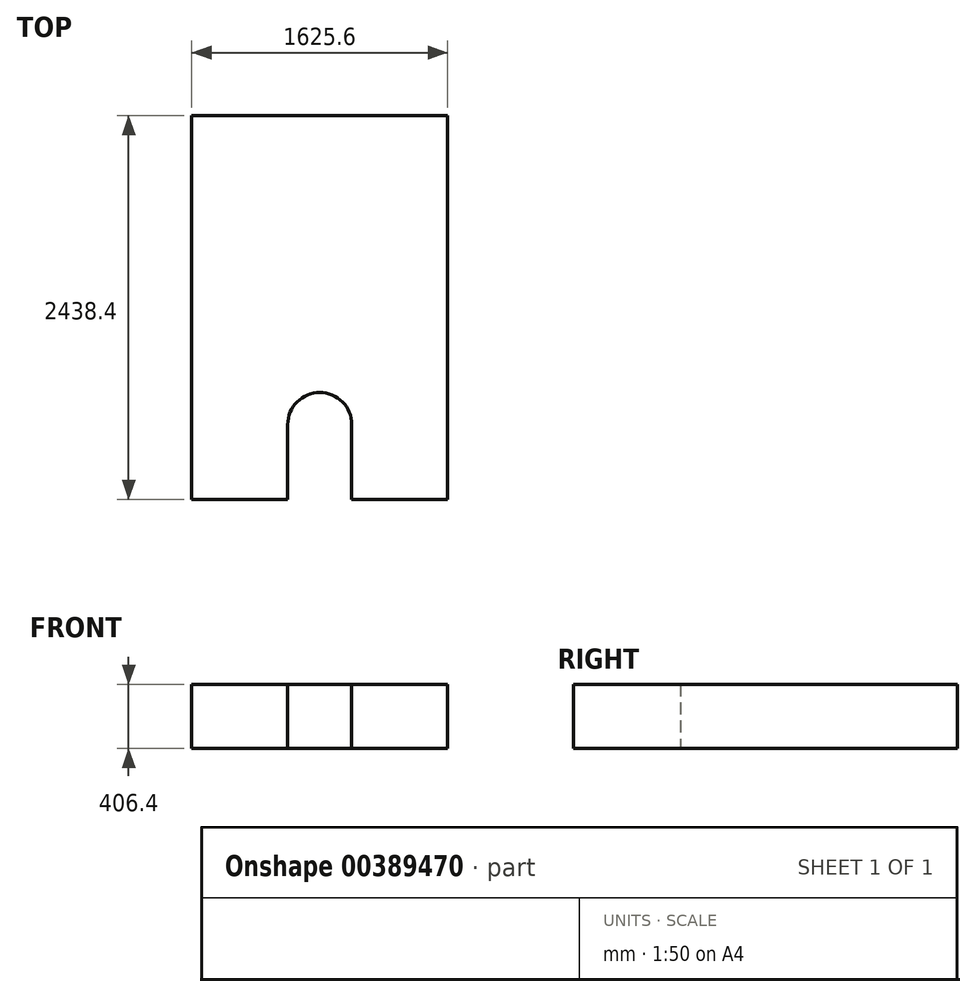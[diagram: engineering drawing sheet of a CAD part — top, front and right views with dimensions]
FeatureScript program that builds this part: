
annotation { "Feature Type Name" : "Feature", "Feature Type Description" : "" }
export const myFeature = defineFeature(function(context is Context, id is Id, definition is map)
    precondition{}
    {
        {
            var Q0;
            Q0=qCreatedBy(makeId("Top.planeOp"),FACE);
            var sketch = newSketch(context, id + "F0", { "sketchPlane" : qUnion([Q0])});
            skLineSegment(sketch, "E0", {"start": v(0, 0) * mm, "end": v(609.6, 0) * mm});
            skLineSegment(sketch, "E1", {"start": v(1625.6, 0) * mm, "end": v(1625.6, 2438.4) * mm});
            skLineSegment(sketch, "E2", {"start": v(1625.6, 2438.4) * mm, "end": v(0, 2438.4) * mm});
            skLineSegment(sketch, "E3", {"start": v(0, 2438.4) * mm, "end": v(0, 0) * mm});
            skLineSegment(sketch, "E4", {"start": v(609.6, 0) * mm, "end": v(609.6, 508) * mm});
            skLineSegment(sketch, "E5", {"start": v(1016, 0) * mm, "end": v(1016, 508) * mm});
            skArc(sketch, "E6", {"start": v(1016, 475.61) * mm, "mid": v(812.8, 678.81) * mm, "end": v(609.6, 475.61) * mm});
            skLineSegment(sketch, "E7.trimOffspring", {"start": v(1016, 0) * mm, "end": v(1625.6, 0) * mm});
            skSolve(sketch);
        }
        {
            var Q0;
            Q0 = qSketchRegion(id + "F0", true);
            var Q1;
            {var subQ0=sQuery(id+"F0.wireOp",EDGE,"E0");Q1=makeQuery(id+"F0.imprint","IMPRINT",FACE,{"disambiguationData":[TD([[makeQuery(id+"F0.imprint","IMPRINT",EDGE,{"derivedFrom":subQ0}),1.0]])]});}
            extrude(context, id + "F1", {"entities" : qUnion([Q0, Q1]), "depth" : 406.4 * mm});
        }
    });
